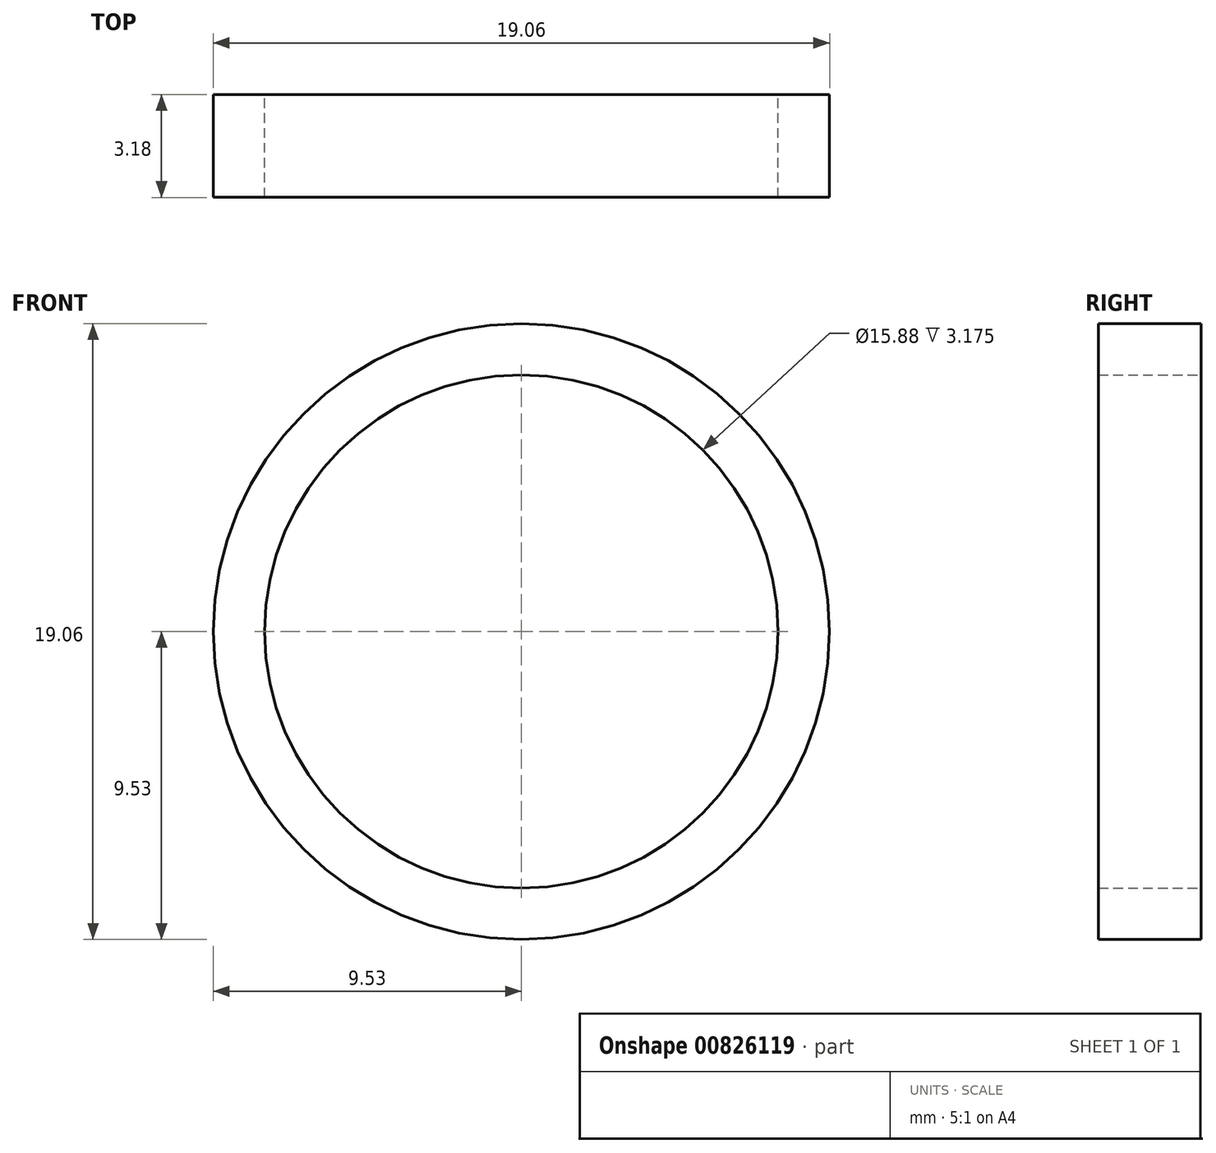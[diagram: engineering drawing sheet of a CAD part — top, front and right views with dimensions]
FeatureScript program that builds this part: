
annotation { "Feature Type Name" : "Feature", "Feature Type Description" : "" }
export const myFeature = defineFeature(function(context is Context, id is Id, definition is map)
    precondition{}
    {
        {
            var Q0;
            Q0=qCreatedBy(makeId("Front.planeOp"),FACE);
            var sketch = newSketch(context, id + "F0", { "sketchPlane" : qUnion([Q0])});
            skCircle(sketch, "E0", {"center": v(0, 0) * mm, "radius": 9.53 * mm});
            skCircle(sketch, "E1", {"center": v(0, 0) * mm, "radius": 7.94 * mm});
            skSolve(sketch);
        }
        {
            var Q0;
            Q0=qSketchRegion(id+"F0",true);
            extrude(context, id + "F1", {"entities" : qUnion([Q0]), "depth" : 3.17 * mm, "offsetDistance" : 25.4 * mm});
        }
    });
